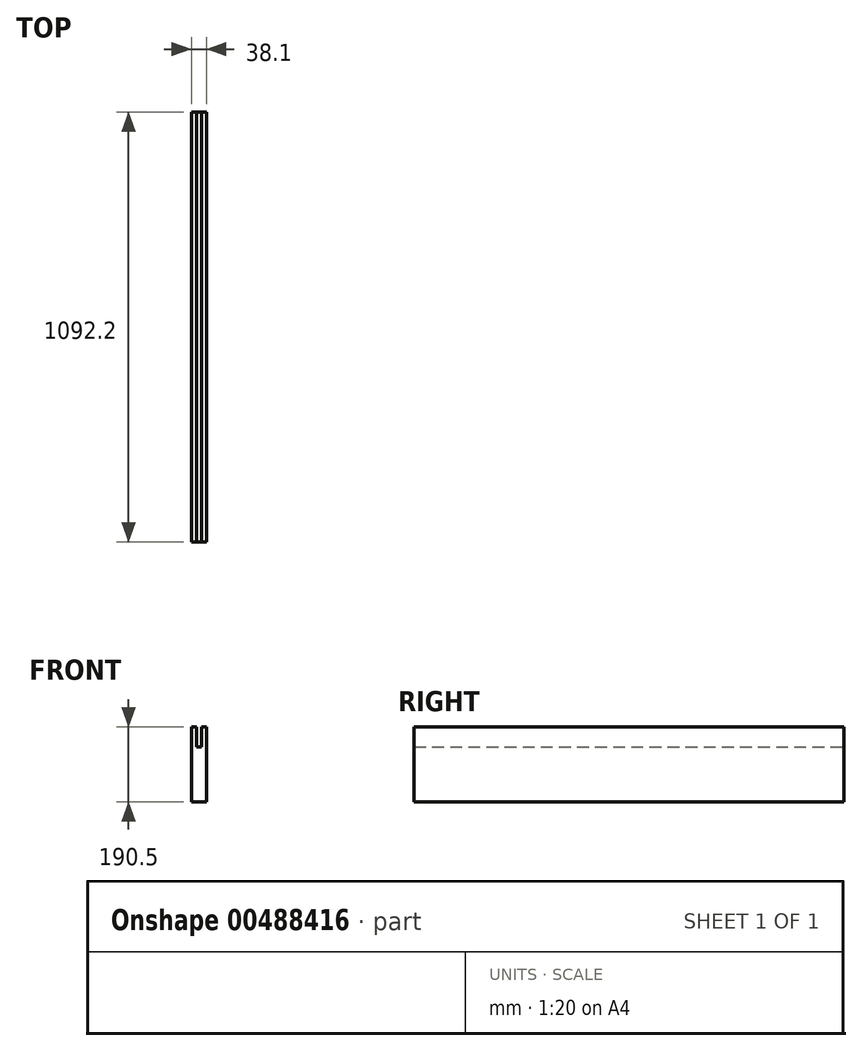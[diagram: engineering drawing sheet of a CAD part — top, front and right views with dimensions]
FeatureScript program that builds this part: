
annotation { "Feature Type Name" : "Feature", "Feature Type Description" : "" }
export const myFeature = defineFeature(function(context is Context, id is Id, definition is map)
    precondition{}
    {
        {
            var Q0;
            Q0=qCreatedBy(makeId("Front.planeOp"),FACE);
            var sketch = newSketch(context, id + "F0", { "sketchPlane" : qUnion([Q0])});
            skLineSegment(sketch, "E0.bottom", {"start": v(19.05, 95.25) * mm, "end": v(6.35, 95.25) * mm});
            skLineSegment(sketch, "E0.left", {"start": v(19.05, 95.25) * mm, "end": v(19.05, -95.25) * mm});
            skLineSegment(sketch, "E0.right", {"start": v(-19.05, 95.25) * mm, "end": v(-19.05, -95.25) * mm});
            skPoint(sketch, "E0.middle", {"position": v(0, 0) * mm});
            skLineSegment(sketch, "E1.top", {"start": v(-6.35, 44.45) * mm, "end": v(6.35, 44.45) * mm});
            skLineSegment(sketch, "E1.left", {"start": v(-6.35, 95.25) * mm, "end": v(-6.35, 44.45) * mm});
            skLineSegment(sketch, "E1.right", {"start": v(6.35, 95.25) * mm, "end": v(6.35, 44.45) * mm});
            skLineSegment(sketch, "E2.trimOffspring", {"start": v(-6.35, 95.25) * mm, "end": v(-19.05, 95.25) * mm});
            skLineSegment(sketch, "E3", {"start": v(-19.05, -95.25) * mm, "end": v(19.05, -95.25) * mm});
            skSolve(sketch);
        }
        {
            var Q0;
            Q0 = qSketchRegion(id + "F0", true);
            extrude(context, id + "F1", {"entities" : qUnion([Q0]), "flatOperationType" : FlatOperationType.REMOVE, "offsetDistance" : 25.4 * mm, "depth" : 1092.2 * mm, "domain" : OperationDomain.MODEL, "symmetric" : true});
        }
    });
